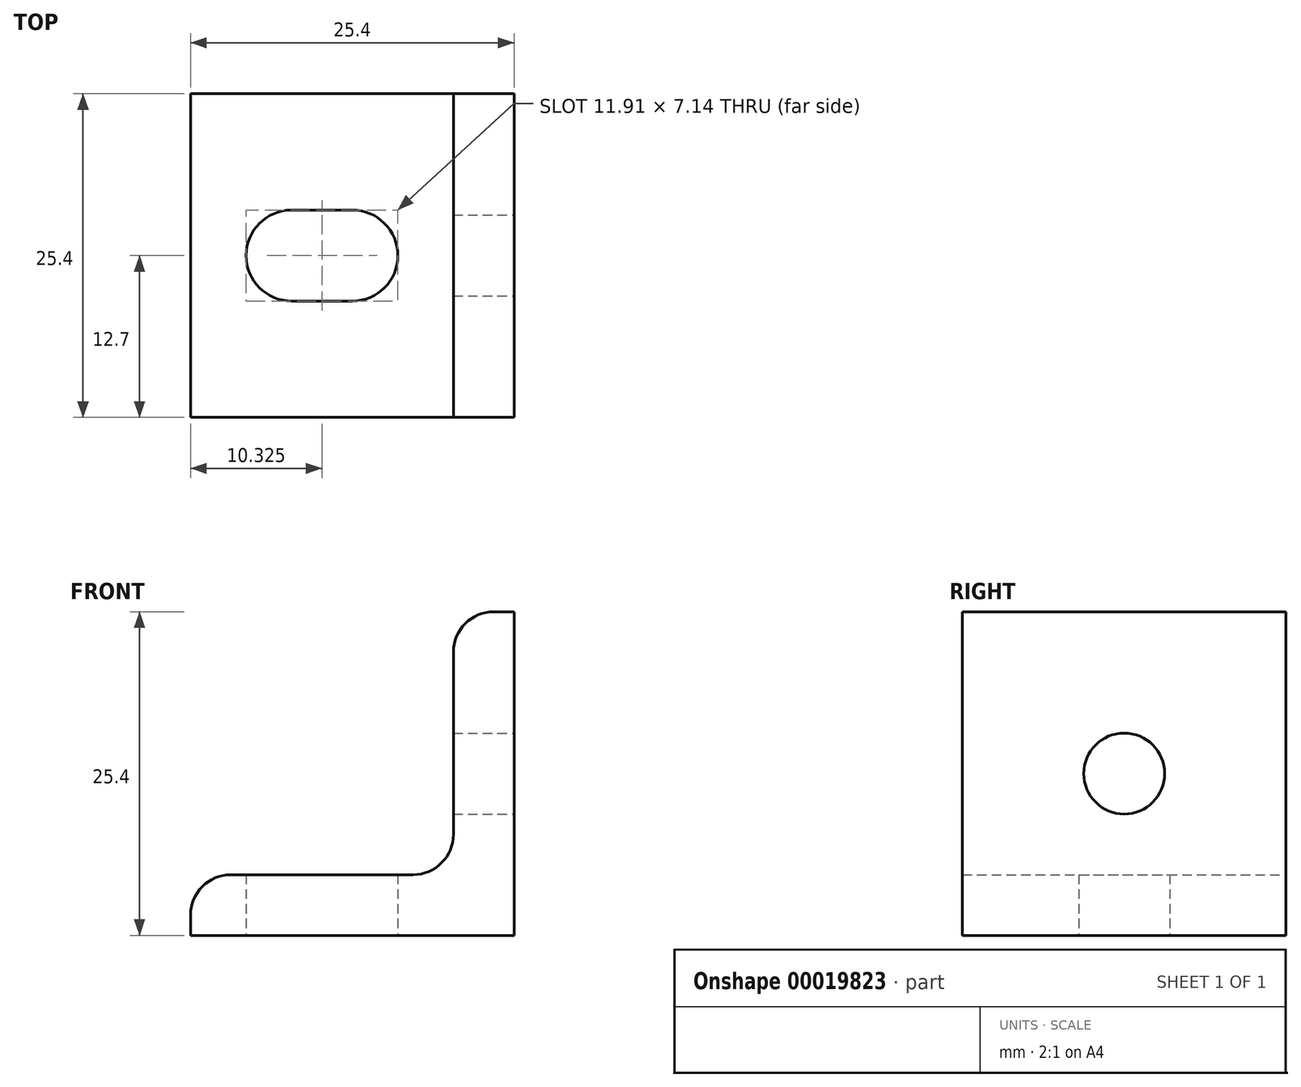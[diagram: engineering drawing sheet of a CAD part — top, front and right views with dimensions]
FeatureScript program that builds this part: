
annotation { "Feature Type Name" : "Feature", "Feature Type Description" : "" }
export const myFeature = defineFeature(function(context is Context, id is Id, definition is map)
    precondition{}
    {
        {
            var Q0;
            Q0=qCreatedBy(makeId("Front.planeOp"),FACE);
            var sketch = newSketch(context, id + "F0", { "sketchPlane" : qUnion([Q0])});
            skLineSegment(sketch, "E0.bottom", {"start": v(0, 0) * mm, "end": v(-25.4, 0) * mm});
            skLineSegment(sketch, "E0.top", {"start": v(0, 25.4) * mm, "end": v(-4.76, 25.4) * mm});
            skLineSegment(sketch, "E0.left", {"start": v(0, 0) * mm, "end": v(0, 25.4) * mm});
            skLineSegment(sketch, "E0.right", {"start": v(-25.4, 0) * mm, "end": v(-25.4, 4.76) * mm});
            skLineSegment(sketch, "E1.top", {"start": v(-25.4, 4.76) * mm, "end": v(-4.76, 4.76) * mm});
            skLineSegment(sketch, "E1.right", {"start": v(-4.76, 25.4) * mm, "end": v(-4.76, 4.76) * mm});
            skSolve(sketch);
        }
        {
            var Q0;
            Q0=makeQuery(id+"F0.imprint","IMPRINT",FACE,{"disambiguationData":[TD([[makeQuery(id+"F0.imprint","IMPRINT",EDGE,{"derivedFrom":sQuery(id+"F0.wireOp",EDGE,"E0.bottom")}),-1.0]])]});
            extrude(context, id + "F1", {"entities" : qUnion([Q0]), "endBound" : BoundingType.SYMMETRIC, "depth" : 25.4 * mm});
        }
        {
            var Q0;
            Q0=makeQuery(id+"F1.opExtrude","SWEPT_EDGE",EDGE,{"disambiguationData":[OSD([sQuery(id+"F0.wireOp",EDGE,"E0.top"),sQuery(id+"F0.wireOp",EDGE,"E1.right")])]});
            var Q1;
            Q1=makeQuery(id+"F1.opExtrude","SWEPT_EDGE",EDGE,{"disambiguationData":[OSD([sQuery(id+"F0.wireOp",EDGE,"E0.right"),sQuery(id+"F0.wireOp",EDGE,"E1.top")])]});
            fillet(context, id + "F2", {"entities" : qUnion([Q0, Q1]), "radius" : 3.17 * mm, "tangentPropagation" : true, "allowEdgeOverflow" : false});
        }
        {
            var Q0;
            Q0=makeQuery(id+"F1.opExtrude","SWEPT_FACE",FACE,{"disambiguationData":[OSD([sQuery(id+"F0.wireOp",EDGE,"E0.left")])]});
            var sketch = newSketch(context, id + "F3", { "sketchPlane" : qUnion([Q0])});
            skPoint(sketch, "E2", {"position": v(0, 12.7) * mm});
            skLineSegment(sketch, "E3", {"start": v(0, 0) * mm, "end": v(0, 12.7) * mm});
            skSolve(sketch);
        }
        {
            var Q0;
            Q0=sQuery(id+"F3.wireOp",VERTEX,"E2");
            var Q1;
            Q1=makeQuery(id+"F1.opExtrude","SWEPT_BODY",BODY,{"disambiguationData":[OSD([sQuery(id+"F0.wireOp",EDGE,"E0.bottom"),sQuery(id+"F0.wireOp",EDGE,"E0.top"),sQuery(id+"F0.wireOp",EDGE,"E0.left"),sQuery(id+"F0.wireOp",EDGE,"E0.right"),sQuery(id+"F0.wireOp",EDGE,"E1.top"),sQuery(id+"F0.wireOp",EDGE,"E1.right")])]});
            hole(context, id + "F4", {"style" : HoleStyle.SIMPLE, "holeDiameter" : 6.35 * mm, "endStyle" : HoleEndStyle.THROUGH, "locations" : qUnion([Q0]), "scope" : qUnion([Q1])});
        }
        {
            var Q0;
            Q0=makeQuery(id+"F1.opExtrude","SWEPT_FACE",FACE,{"disambiguationData":[OSD([sQuery(id+"F0.wireOp",EDGE,"E0.bottom")])]});
            var sketch = newSketch(context, id + "F5", { "sketchPlane" : qUnion([Q0])});
            skPoint(sketch, "E4", {"position": v(-15.07, 0) * mm});
            skLineSegment(sketch, "E5", {"start": v(0, 0) * mm, "end": v(-15.07, 0) * mm});
            skLineSegment(sketch, "E6.rect.bottom", {"start": v(-17.46, 3.57) * mm, "end": v(-12.69, 3.57) * mm});
            skLineSegment(sketch, "E6.rect.top", {"start": v(-17.46, -3.57) * mm, "end": v(-12.69, -3.57) * mm});
            skLineSegment(sketch, "E6.rect.left", {"start": v(-21.03, 0) * mm, "end": v(-21.03, 0) * mm});
            skLineSegment(sketch, "E6.rect.right", {"start": v(-9.12, 0) * mm, "end": v(-9.12, 0) * mm});
            skPoint(sketch, "E7.visualSharp", {"position": v(-21.03, 3.57) * mm});
            skArc(sketch, "E7.filletArc", {"start": v(-17.46, 3.57) * mm, "mid": v(-19.99, 2.52) * mm, "end": v(-21.03, 0) * mm});
            skPoint(sketch, "E8.visualSharp", {"position": v(-21.03, -3.57) * mm});
            skArc(sketch, "E8.filletArc", {"start": v(-21.03, 0) * mm, "mid": v(-19.99, -2.52) * mm, "end": v(-17.46, -3.57) * mm});
            skPoint(sketch, "E9.visualSharp", {"position": v(-9.12, -3.57) * mm});
            skArc(sketch, "E9.filletArc", {"start": v(-12.69, -3.57) * mm, "mid": v(-10.16, -2.52) * mm, "end": v(-9.12, 0) * mm});
            skPoint(sketch, "E10.visualSharp", {"position": v(-9.12, 3.57) * mm});
            skArc(sketch, "E10.filletArc", {"start": v(-9.12, 0) * mm, "mid": v(-10.16, 2.52) * mm, "end": v(-12.69, 3.57) * mm});
            skSolve(sketch);
        }
        {
            var Q0;
            Q0=makeQuery(id+"F1.opExtrude","SWEPT_EDGE",EDGE,{"disambiguationData":[OSD([sQuery(id+"F0.wireOp",EDGE,"E1.top"),sQuery(id+"F0.wireOp",EDGE,"E1.right")])]});
            fillet(context, id + "F6", {"entities" : qUnion([Q0]), "radius" : 3.17 * mm, "tangentPropagation" : true, "allowEdgeOverflow" : false});
        }
        {
            var Q0;
            Q0=makeQuery(id+"F5.imprint","IMPRINT",FACE,{"disambiguationData":[TD([[makeQuery(id+"F5.imprint","IMPRINT",EDGE,{"derivedFrom":sQuery(id+"F5.wireOp",EDGE,"E6.rect.bottom")}),-1.0]])]});
            extrude(context, id + "F7", {"entities" : qUnion([Q0]), "operationType" : NewBodyOperationType.REMOVE, "endBound" : BoundingType.THROUGH_ALL, "oppositeDirection" : true, "depth" : 25.4 * mm});
        }
    });
